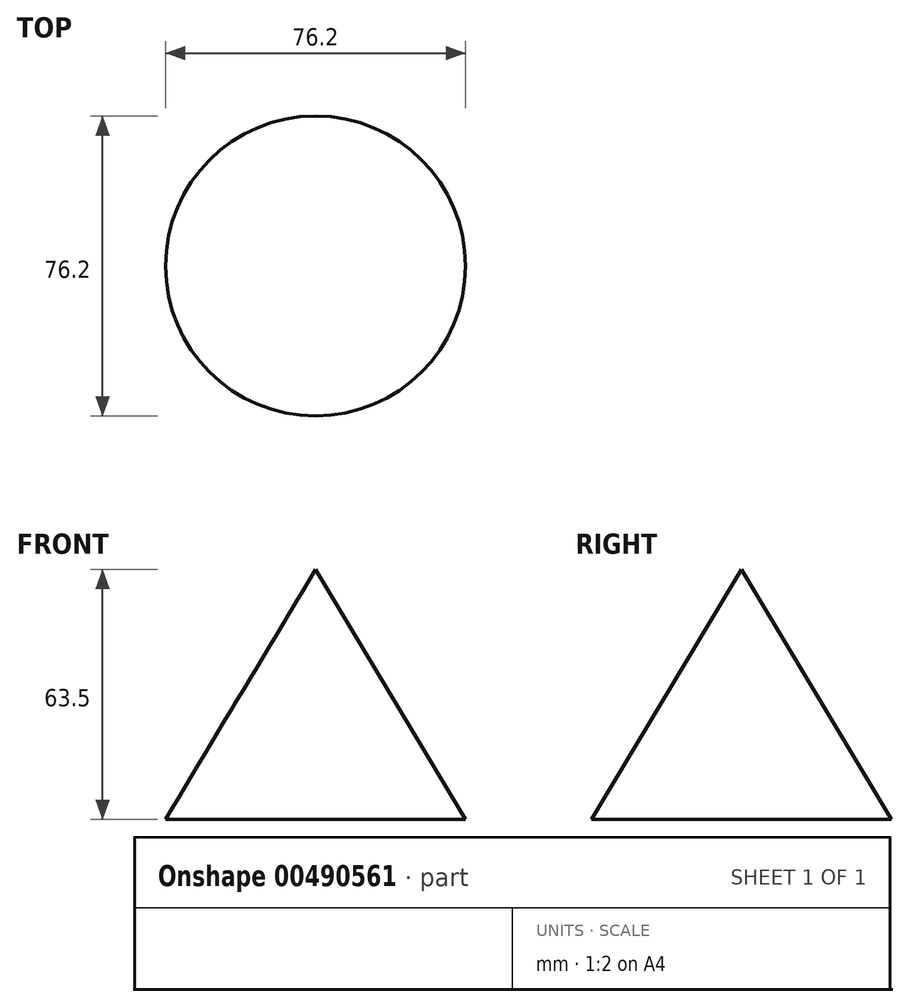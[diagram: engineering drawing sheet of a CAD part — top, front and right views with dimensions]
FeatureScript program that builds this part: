
annotation { "Feature Type Name" : "Feature", "Feature Type Description" : "" }
export const myFeature = defineFeature(function(context is Context, id is Id, definition is map)
    precondition{}
    {
        {
            var Q0;
            Q0=qCreatedBy(makeId("Front.planeOp"),FACE);
            var sketch = newSketch(context, id + "F0", { "sketchPlane" : qUnion([Q0])});
            skLineSegment(sketch, "E0", {"start": v(0, 0) * mm, "end": v(-38.1, 0) * mm});
            skLineSegment(sketch, "E1", {"start": v(-38.1, 0) * mm, "end": v(0, 63.5) * mm});
            skLineSegment(sketch, "E2", {"start": v(0, 63.5) * mm, "end": v(0, 0) * mm});
            skSolve(sketch);
        }
        {
            var Q0;
            Q0 = qSketchRegion(id + "F0", true);
            var Q1;
            Q1=sQuery(id+"F0.wireOp",EDGE,"E0");
            var Q2;
            Q2=sQuery(id+"F0.wireOp",EDGE,"E1");
            var Q3;
            Q3=sQuery(id+"F0.wireOp",EDGE,"E2");
            var Q4;
            Q4=sQuery(id+"F0.wireOp",EDGE,"E2");
            revolve(context, id + "F1", {"entities" : qUnion([Q0]), "surfaceEntities" : qUnion([Q1, Q2, Q3]), "axis" : qUnion([Q4]), "revolveType" : RevolveType.FULL});
        }
    });
